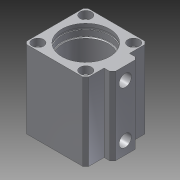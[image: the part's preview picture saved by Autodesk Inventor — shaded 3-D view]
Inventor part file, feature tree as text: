
AUTODESK INVENTOR PART (.ipt)
format: ipt  version: 2016 (Build 200138000, 138)  size: 253,440 bytes
history: native  units: mm
features: sketch x10, extrude x9, chamfer x2, plane x2, hole x2, mirror x1, projected_geometry x1
ambient origin geometry x8: Origin, YZ Plane, XZ Plane, XY Plane, X Axis, Y Axis, Z Axis, Center Point
bodies: Solid1 (feature_tree)
feature tree (27):
  extrude  "Extrusion1"  Depth=44.0mm
  extrude  "Extrusion2"  Depth=6.0mm
  extrude  "Extrusion3"  Depth=55.0mm
  chamfer  "Chamfer1"  Distance=55.0mm
  plane  "Work Plane1"
  extrude  "Extrusion4"  Depth=47.0mm TaperAngle=0.0deg
  extrude  "Extrusion5"  Depth=8.0mm TaperAngle=0.0deg
  extrude  "Extrusion6"  [1 undecoded]
  extrude  "Extrusion7"  Depth=1.5mm TaperAngle=0.0deg
  extrude  "Extrusion8"  Depth=50.0mm
  chamfer  "Chamfer2"  Distance=1.5mm
  extrude  "Extrusion9"  Depth=9.0mm
  plane  "Work Plane2"
  mirror  "Mirror1"
  hole  "Hole2"  [1 undecoded]
  sketch  "Sketch1"  dims[d0=44.0mm d1=44.0mm]
  sketch  "Sketch2"  dims[d2=12.0mm d3=6.0mm]
  sketch  "Sketch3"  dims[d4=34.0mm d5=34.0mm d6=55.0mm d7=0.0mm]
  sketch  "Sketch4"  dims[d8=32.0mm d9=47.0mm d10=0.0mm]
  projected_geometry  "Projected Loop1"
  sketch  "Sketch5"  dims[d11=34.0mm d12=8.0mm d13=0.0mm]
  sketch  "Sketch6"  dims[d14=0.5mm d15=2.0mm d16=45.0deg d17=-4.0mm]
  sketch  "Sketch7"  dims[d18=35.0mm d19=1.5mm d20=0.0mm]
  sketch  "Sketch8"  dims[d21=18.0mm d22=50.0mm d23=1.5mm d24=0.0mm]
  sketch  "Sketch9"  dims[d25=8.75mm d26=9.0mm]
  sketch  "Sketch10"  dims[d27=9.0mm d28=0.0mm d29=46.0mm d30=9.0mm d31=0.0mm d32=3.0mm d33=9.0mm d34=0.0mm d35=2.0mm d36=2.0mm d37=45.0deg d38=8.2mm d39=5.2mm d40=0.0mm d41=4.917mm d42=12.8mm d43=4.0mm d44=2.0mm d45=90.0deg d46=15.8mm d47=120.0deg]
  hole  "Hole1"  [1 undecoded]
note: 3 required parameter values undecoded (feature->parameter linkage not recoverable at this tier; creation-order binding heuristic only, values carry confidence <= 0.55)
